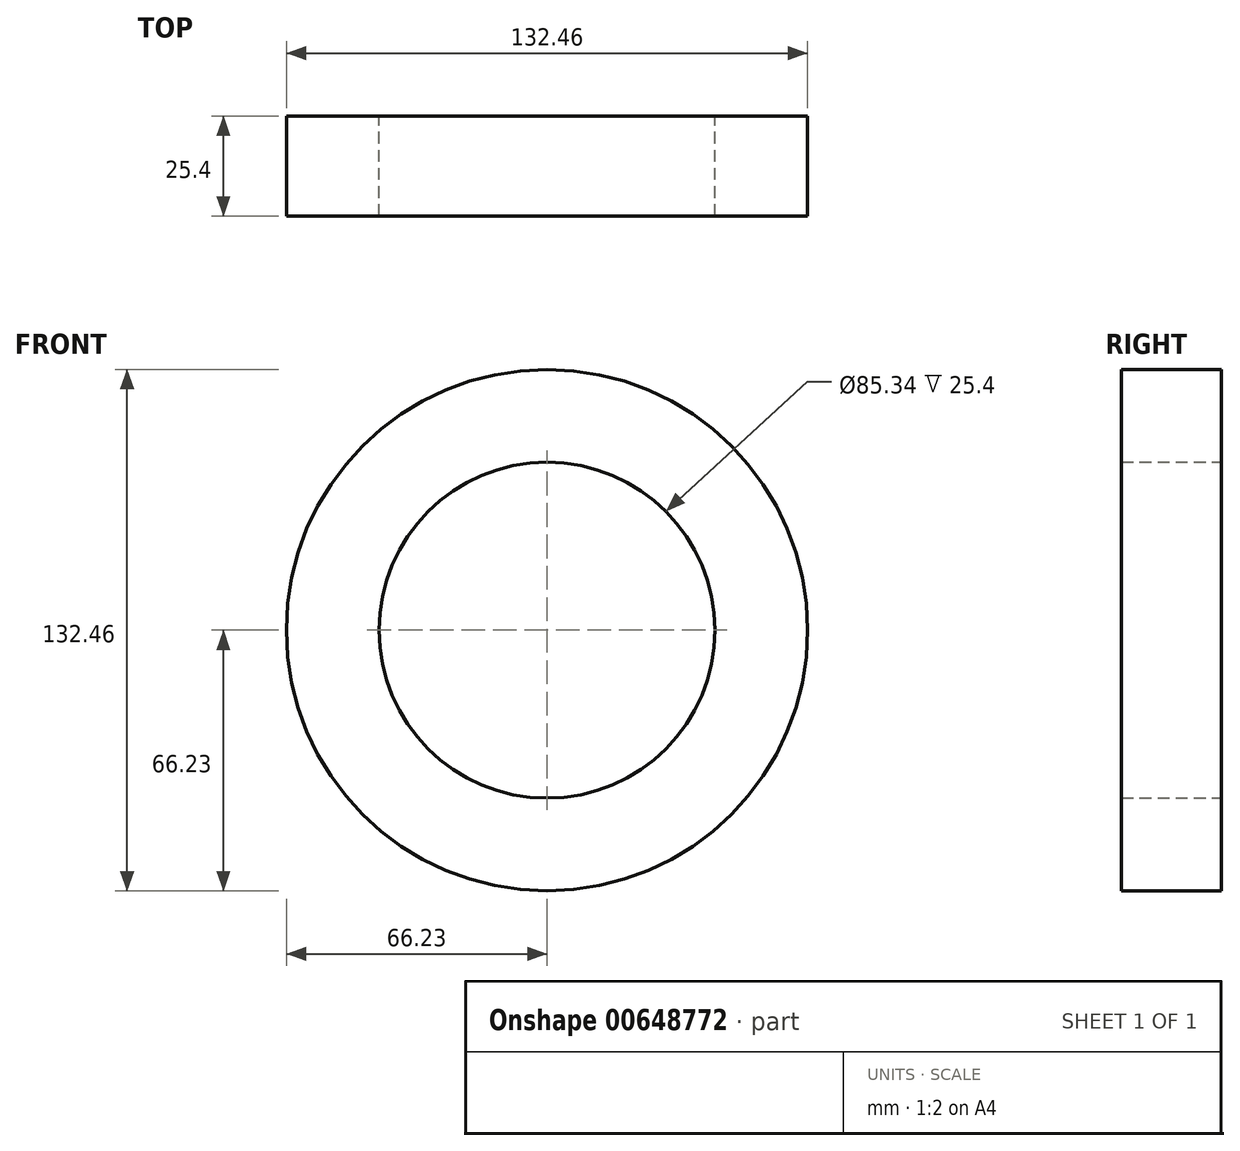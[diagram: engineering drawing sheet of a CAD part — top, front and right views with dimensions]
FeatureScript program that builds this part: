
annotation { "Feature Type Name" : "Feature", "Feature Type Description" : "" }
export const myFeature = defineFeature(function(context is Context, id is Id, definition is map)
    precondition{}
    {
        {
            var Q0;
            Q0=qCreatedBy(makeId("Front.planeOp"),FACE);
            var sketch = newSketch(context, id + "F0", { "sketchPlane" : qUnion([Q0])});
            skCircle(sketch, "E0", {"center": v(0, 0) * mm, "radius": 66.23 * mm});
            skCircle(sketch, "E1", {"center": v(0, 0) * mm, "radius": 42.67 * mm});
            skSolve(sketch);
        }
        {
            var Q0;
            Q0=makeQuery(id+"F0.imprint","IMPRINT",FACE,{"disambiguationData":[TD([[makeQuery(id+"F0.imprint","IMPRINT",EDGE,{"derivedFrom":sQuery(id+"F0.wireOp",EDGE,"E0")}),1.0]])]});
            extrude(context, id + "F1", {"entities" : qUnion([Q0]), "depth" : 25.4 * mm, "offsetDistance" : 25.4 * mm});
        }
    });
